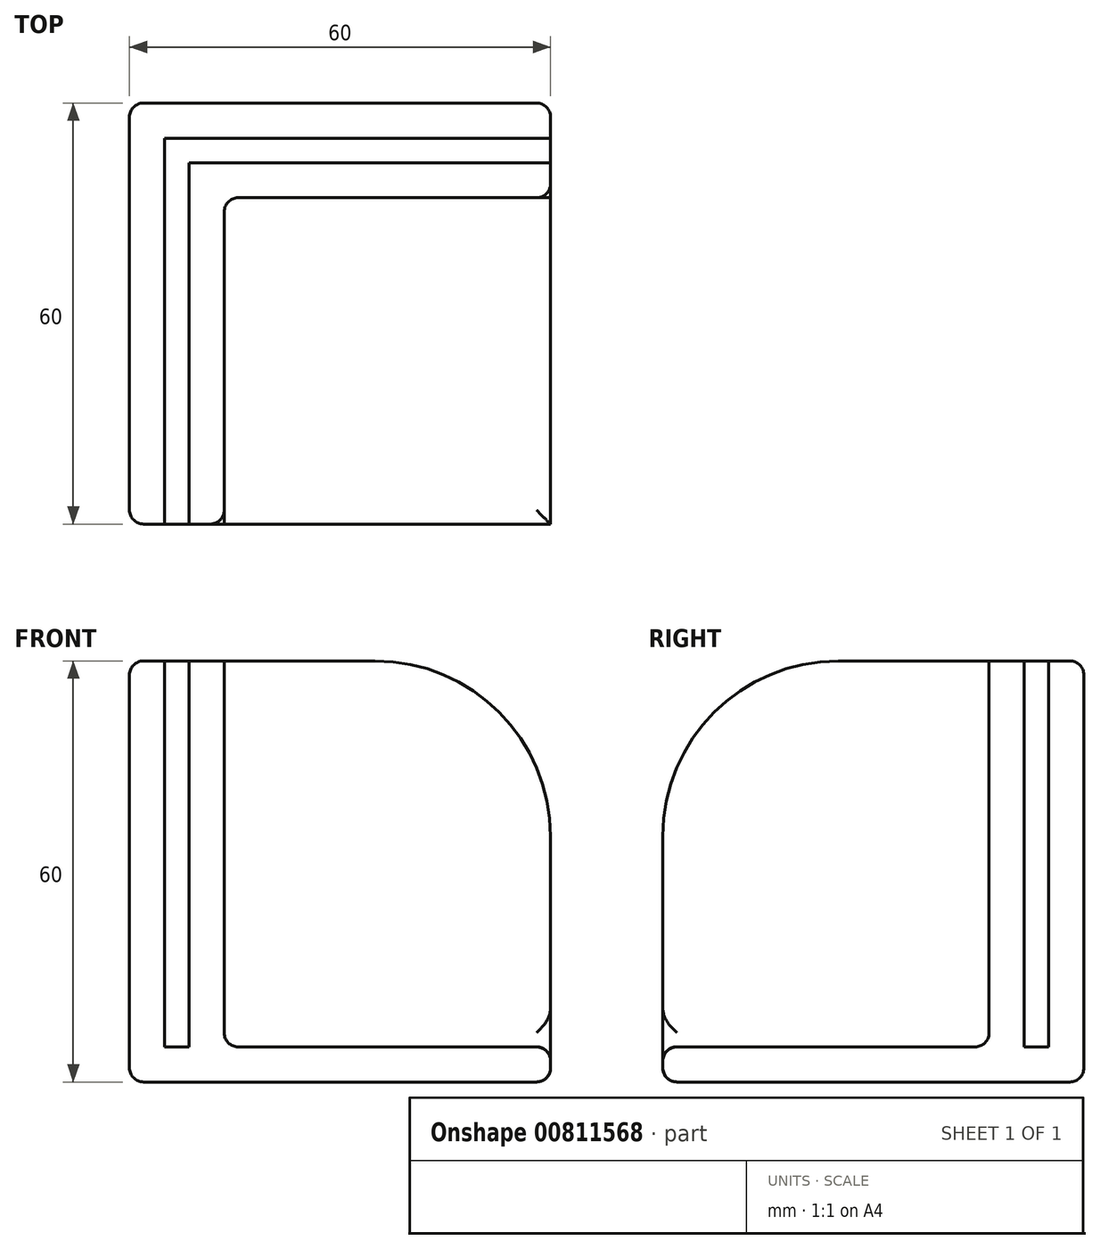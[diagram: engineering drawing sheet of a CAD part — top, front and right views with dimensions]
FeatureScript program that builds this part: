
annotation { "Feature Type Name" : "Feature", "Feature Type Description" : "" }
export const myFeature = defineFeature(function(context is Context, id is Id, definition is map)
    precondition{}
    {
        {
            var Q0;
            Q0=qCreatedBy(makeId("Top.planeOp"),FACE);
            var sketch = newSketch(context, id + "F0", { "sketchPlane" : qUnion([Q0])});
            skLineSegment(sketch, "E0.bottom", {"start": v(30, -30) * mm, "end": v(-30, -30) * mm});
            skLineSegment(sketch, "E0.top", {"start": v(30, 30) * mm, "end": v(-30, 30) * mm});
            skLineSegment(sketch, "E0.left", {"start": v(30, -30) * mm, "end": v(30, 30) * mm});
            skLineSegment(sketch, "E0.right", {"start": v(-30, -30) * mm, "end": v(-30, 30) * mm});
            skPoint(sketch, "E0.middle", {"position": v(0, 0) * mm});
            skSolve(sketch);
        }
        {
            var Q0;
            Q0=qSketchRegion(id+"F0",true);
            extrude(context, id + "F1", {"entities" : qUnion([Q0]), "depth" : 5 * mm, "offsetDistance" : 25 * mm});
        }
        {
            var Q0;
            Q0=makeQuery(id+"F1.opExtrude","CAP_FACE",FACE,{"disambiguationData":[OSD([sQuery(id+"F0.wireOp",EDGE,"E0.bottom"),sQuery(id+"F0.wireOp",EDGE,"E0.top"),sQuery(id+"F0.wireOp",EDGE,"E0.left"),sQuery(id+"F0.wireOp",EDGE,"E0.right")])],"isStart":false});
            var sketch = newSketch(context, id + "F2", { "sketchPlane" : qUnion([Q0])});
            skLineSegment(sketch, "E1.bottom", {"start": v(-30, 30) * mm, "end": v(-25, 30) * mm});
            skLineSegment(sketch, "E1.top", {"start": v(-30, -30) * mm, "end": v(-25, -30) * mm});
            skLineSegment(sketch, "E1.left", {"start": v(-30, 30) * mm, "end": v(-30, -30) * mm});
            skLineSegment(sketch, "E1.right", {"start": v(-25, 30) * mm, "end": v(-25, -30) * mm});
            skLineSegment(sketch, "E2.bottom", {"start": v(-25, 30) * mm, "end": v(30, 30) * mm});
            skLineSegment(sketch, "E2.top", {"start": v(-25, 25) * mm, "end": v(30, 25) * mm});
            skLineSegment(sketch, "E2.left", {"start": v(-25, 30) * mm, "end": v(-25, 25) * mm});
            skLineSegment(sketch, "E2.right", {"start": v(30, 30) * mm, "end": v(30, 25) * mm});
            skSolve(sketch);
        }
        {
            var Q0;
            Q0=qSketchRegion(id+"F2",true);
            extrude(context, id + "F3", {"entities" : qUnion([Q0]), "operationType" : NewBodyOperationType.ADD, "depth" : 55 * mm, "offsetDistance" : 25 * mm});
        }
        {
            var Q0;
            Q0=makeQuery(id+"F1.opExtrude","CAP_FACE",FACE,{"disambiguationData":[OSD([sQuery(id+"F0.wireOp",EDGE,"E0.bottom"),sQuery(id+"F0.wireOp",EDGE,"E0.top"),sQuery(id+"F0.wireOp",EDGE,"E0.left"),sQuery(id+"F0.wireOp",EDGE,"E0.right")])],"isStart":false});
            var sketch = newSketch(context, id + "F4", { "sketchPlane" : qUnion([Q0])});
            skLineSegment(sketch, "E3.bottom", {"start": v(-21.5, -30) * mm, "end": v(-16.5, -30) * mm});
            skLineSegment(sketch, "E3.top", {"start": v(-21.5, 21.5) * mm, "end": v(-16.5, 21.5) * mm});
            skLineSegment(sketch, "E3.left", {"start": v(-21.5, -30) * mm, "end": v(-21.5, 21.5) * mm});
            skLineSegment(sketch, "E3.right", {"start": v(-16.5, -30) * mm, "end": v(-16.5, 21.5) * mm});
            skLineSegment(sketch, "E4.bottom", {"start": v(-16.5, 21.5) * mm, "end": v(30, 21.5) * mm});
            skLineSegment(sketch, "E4.top", {"start": v(-16.5, 16.5) * mm, "end": v(30, 16.5) * mm});
            skLineSegment(sketch, "E4.left", {"start": v(-16.5, 21.5) * mm, "end": v(-16.5, 16.5) * mm});
            skLineSegment(sketch, "E4.right", {"start": v(30, 21.5) * mm, "end": v(30, 16.5) * mm});
            skSolve(sketch);
        }
        {
            var Q0;
            Q0=qSketchRegion(id+"F4",true);
            var Q1;
            Q1=makeQuery(id+"F3.opExtrude","CAP_FACE",FACE,{"disambiguationData":[OSD([sQuery(id+"F2.wireOp",EDGE,"E1.bottom"),sQuery(id+"F2.wireOp",EDGE,"E1.top"),sQuery(id+"F2.wireOp",EDGE,"E1.left"),sQuery(id+"F2.wireOp",EDGE,"E1.right"),sQuery(id+"F2.wireOp",EDGE,"E2.bottom"),sQuery(id+"F2.wireOp",EDGE,"E2.top"),sQuery(id+"F2.wireOp",EDGE,"E2.right")])],"isStart":false});
            extrude(context, id + "F5", {"entities" : qUnion([Q0]), "operationType" : NewBodyOperationType.ADD, "endBound" : BoundingType.UP_TO_SURFACE, "depth" : 25 * mm, "endBoundEntityFace" : qUnion([Q1]), "offsetDistance" : 25 * mm});
        }
        {
            var Q0;
            Q0=makeQuery(id+"F3.opExtrude","CAP_EDGE",EDGE,{"disambiguationData":[OSD([sQuery(id+"F2.wireOp",EDGE,"E1.top")])],"isStart":false});
            var Q1;
            Q1=makeQuery(id+"F5.opExtrude","CAP_EDGE",EDGE,{"disambiguationData":[OSD([sQuery(id+"F4.wireOp",EDGE,"E3.bottom")])],"isStart":false});
            var Q2;
            Q2=makeQuery(id+"F5.opExtrude","CAP_EDGE",EDGE,{"disambiguationData":[OSD([sQuery(id+"F4.wireOp",EDGE,"E4.right")])],"isStart":false});
            var Q3;
            Q3=makeQuery(id+"F3.opExtrude","CAP_EDGE",EDGE,{"disambiguationData":[OSD([sQuery(id+"F2.wireOp",EDGE,"E2.right")])],"isStart":false});
            fillet(context, id + "F6", {"entities" : qUnion([Q0, Q1, Q2, Q3]), "radius" : 25 * mm, "tangentPropagation" : true, "allowEdgeOverflow" : false});
        }
        {
            var Q0;
            Q0=makeQuery(id+"F3.boolean.opBoolean","MERGE",FACE,{"derivedFrom":[makeQuery(id+"F1.opExtrude","SWEPT_FACE",FACE,{"disambiguationData":[OSD([sQuery(id+"F0.wireOp",EDGE,"E0.top")])]}),makeQuery(id+"F3.opExtrude","SWEPT_FACE",FACE,{"disambiguationData":[OSD([sQuery(id+"F2.wireOp",EDGE,"E1.bottom"),sQuery(id+"F2.wireOp",EDGE,"E2.bottom")])]})]});
            var Q1;
            Q1=makeQuery(id+"F1.opExtrude","CAP_FACE",FACE,{"disambiguationData":[OSD([sQuery(id+"F0.wireOp",EDGE,"E0.bottom"),sQuery(id+"F0.wireOp",EDGE,"E0.top"),sQuery(id+"F0.wireOp",EDGE,"E0.left"),sQuery(id+"F0.wireOp",EDGE,"E0.right")])],"isStart":true});
            var Q2;
            Q2=makeQuery(id+"F3.boolean.opBoolean","MERGE",FACE,{"derivedFrom":[makeQuery(id+"F1.opExtrude","SWEPT_FACE",FACE,{"disambiguationData":[OSD([sQuery(id+"F0.wireOp",EDGE,"E0.right")])]}),makeQuery(id+"F3.opExtrude","SWEPT_FACE",FACE,{"disambiguationData":[OSD([sQuery(id+"F2.wireOp",EDGE,"E1.left")])]})]});
            var Q3;
            {var subQ0=sQuery(id+"F0.wireOp",EDGE,"E0.left");var subQ1=sQuery(id+"F0.wireOp",EDGE,"E0.bottom");Q3=makeQuery(id+"F5.boolean.opBoolean","SPLIT",FACE,{"disambiguationData":[TD([makeQuery(id+"F5.opExtrude","SWEPT_FACE",FACE,{"disambiguationData":[OSD([sQuery(id+"F4.wireOp",EDGE,"E3.right")])]})])],"derivedFrom":makeQuery(id+"F1.opExtrude","CAP_FACE",FACE,{"disambiguationData":[OSD([subQ1,sQuery(id+"F0.wireOp",EDGE,"E0.top"),subQ0,sQuery(id+"F0.wireOp",EDGE,"E0.right")])],"isStart":false})});}
            var Q4;
            Q4=makeQuery(id+"F5.opExtrude","SWEPT_EDGE",EDGE,{"disambiguationData":[OSD([sQuery(id+"F4.wireOp",EDGE,"E3.right"),sQuery(id+"F4.wireOp",EDGE,"E4.top"),sQuery(id+"F4.wireOp",EDGE,"E4.left")])]});
            fillet(context, id + "F7", {"entities" : qUnion([Q0, Q1, Q2, Q3, Q4]), "radius" : 2 * mm, "tangentPropagation" : true, "allowEdgeOverflow" : false});
        }
    });
